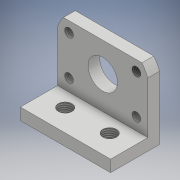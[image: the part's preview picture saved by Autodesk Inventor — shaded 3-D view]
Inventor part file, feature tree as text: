
AUTODESK INVENTOR PART (.ipt)
format: ipt  version: 2018 (Build 220112000, 112)  size: 166,400 bytes
history: native  units: mm
features: thread x7, sketch x6, extrude x3, hole x3
ambient origin geometry x8: Origin, YZ Plane, XZ Plane, XY Plane, X Axis, Y Axis, Z Axis, Center Point
bodies: Solid1 (feature_tree)
feature tree (19):
  extrude  "Extrusion1"  Depth=25.0mm
  hole  "Hole1"  [1 undecoded]
  extrude  "Extrusion2"  Depth=6.0mm
  hole  "Hole2"  [1 undecoded]
  hole  "Hole3"  [1 undecoded]
  extrude  "Extrusion3"  Depth=10.0mm
  thread  "Thread5"  [1 undecoded]
  thread  "Thread6"  [1 undecoded]
  thread  "Thread7"  [1 undecoded]
  thread  "Thread8"  [1 undecoded]
  thread  "Thread9"  [1 undecoded]
  thread  "Thread10"  [1 undecoded]
  thread  "Thread11"  [1 undecoded]
  sketch  "Sketch1"  dims[d0=46.0mm d1=25.0mm]
  sketch  "Sketch2"  dims[d2=6.0mm d3=0.0mm d5=13.8mm]
  sketch  "Sketch3"  dims[d6=7.0mm d7=6.0mm d8=4.0mm d9=2.0mm d10=90.0deg d11=8.0mm d12=20.594885mm d13=6.0mm]
  sketch  "Sketch4"  dims[d14=31.55mm d15=0.0mm d16=12.254mm]
  sketch  "Sketch5"  dims[d17=5.824mm d18=20.0mm]
  sketch  "Sketch6"  dims[d19=4.5mm d20=6.0mm d21=4.0mm d22=2.0mm d23=90.0deg d24=6.0mm d25=20.594885mm d26=15.0mm d27=15.0mm d28=6.0mm d29=4.0mm d30=2.0mm d31=90.0deg d32=6.0mm d33=20.594885mm d34=11.65mm d35=50.0mm d36=23.55mm d37=0.0mm d46=10.0mm d47=0.0mm d48=10.0mm d49=0.0mm d50=10.0mm d51=0.0mm d52=10.0mm d53=0.0mm d54=10.0mm d55=0.0mm d56=10.0mm d57=0.0mm d58=10.0mm d59=0.0mm]
note: 10 required parameter values undecoded (feature->parameter linkage not recoverable at this tier; creation-order binding heuristic only, values carry confidence <= 0.55)
